# Revit family: Justerbar Optimus
name_source: partatom
category: Lighting Fixtures
units: mm (PartAtom-declared; Revit-internal decimal feet)

## family parameters
Always vertical = Yes
Cut with Voids When Loaded = No
Light Source = Yes
OmniClass Number = 23.80.70.00
OmniClass Title = Lighting
Part Type = Normal
Room Calculation Point = No
Round Connector Dimension = Use Diameter
Shared = No
Work Plane-Based = No

## types (1)
- Justerbar Optimus
    Beskyttelsesglass = Linse
    Beskyttelsesgrad = IP21
    CRI = >80
    Color Filter = 16777215
    Default Elevation = 0 mm  [stored 0 ft]
    Dimbar = Dali på forespørsel
    Dimming Lamp Color Temperature Shift = <None>
    Emit from Line Length = 610 mm
    Farger = Grå
    Fargetemperatur = 4000K
    Kjøle metode = Passiv
    Levetid = L70 50.000 timer
    Light Source Symbol Size = 610 mm
    Lumen = 7500lm
    Lyskilde = LED
    MacAdams = < 3
    Spredning = 60
    Systemeffekt = 65W (1200mA)

note: [stored X ft] marks values corroborated as IEEE doubles in the binary element streams (Revit-internal decimal feet)

## geometry (parser evidence)
native form markers: Sweep x2
no freeform markers — native parametric forms only
